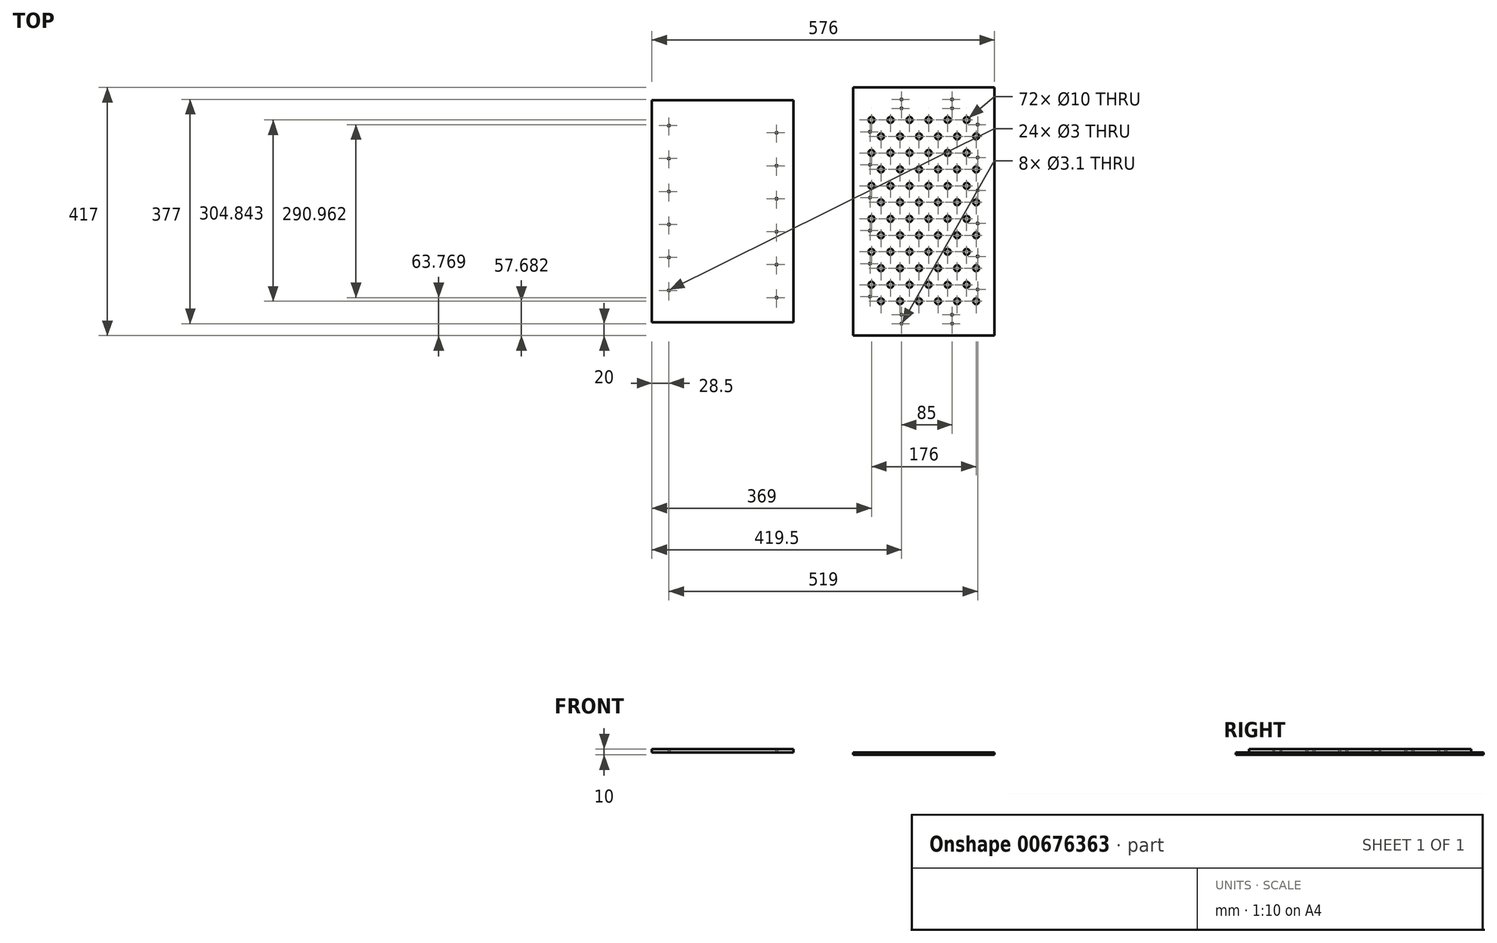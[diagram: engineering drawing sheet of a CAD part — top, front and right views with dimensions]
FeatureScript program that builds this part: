
annotation { "Feature Type Name" : "Feature", "Feature Type Description" : "" }
export const myFeature = defineFeature(function(context is Context, id is Id, definition is map)
    precondition{}
    {
        {
            var Q0;
            Q0=qCreatedBy(makeId("Top.planeOp"),FACE);
            var sketch = newSketch(context, id + "F0", { "sketchPlane" : qUnion([Q0])});
            skLineSegment(sketch, "E0.bottom", {"start": v(119, -186.75) * mm, "end": v(-119, -186.75) * mm});
            skLineSegment(sketch, "E0.top", {"start": v(119, 186.75) * mm, "end": v(-119, 186.75) * mm});
            skLineSegment(sketch, "E0.left", {"start": v(119, -186.75) * mm, "end": v(119, 186.75) * mm});
            skLineSegment(sketch, "E0.right", {"start": v(-119, -186.75) * mm, "end": v(-119, 186.75) * mm});
            skPoint(sketch, "E0.middle", {"position": v(0, 0) * mm});
            skCircle(sketch, "E1", {"center": v(-90.5, -133.36) * mm, "radius": 1.5 * mm});
            skCircle(sketch, "E2", {"center": v(-90.5, -77.93) * mm, "radius": 1.5 * mm});
            skCircle(sketch, "E3", {"center": v(90.5, -145.48) * mm, "radius": 1.5 * mm});
            skCircle(sketch, "E4", {"center": v(90.5, -90.06) * mm, "radius": 1.5 * mm});
            skPoint(sketch, "E5.endSnap0", {"position": v(0, 186.75) * mm});
            skCircle(sketch, "E6.0.1.0", {"center": v(-90.5, -22.5) * mm, "radius": 1.5 * mm});
            skCircle(sketch, "E6.0.2.0", {"center": v(-90.5, 32.92) * mm, "radius": 1.5 * mm});
            skCircle(sketch, "E6.0.3.0", {"center": v(-90.5, 88.34) * mm, "radius": 1.5 * mm});
            skCircle(sketch, "E6.0.4.0", {"center": v(-90.5, 143.77) * mm, "radius": 1.5 * mm});
            skLineSegment(sketch, "E6.direction1", {"start": v(-90.5, -77.93) * mm, "end": v(-65.5, -77.93) * mm, "construction": true});
            skLineSegment(sketch, "E6.direction2", {"start": v(-90.5, -77.93) * mm, "end": v(-90.5, -22.5) * mm, "construction": true});
            skCircle(sketch, "E7.0.1.0", {"center": v(90.5, -34.63) * mm, "radius": 1.5 * mm});
            skCircle(sketch, "E7.0.2.0", {"center": v(90.5, 20.8) * mm, "radius": 1.5 * mm});
            skCircle(sketch, "E7.0.3.0", {"center": v(90.5, 76.22) * mm, "radius": 1.5 * mm});
            skCircle(sketch, "E7.0.4.0", {"center": v(90.5, 131.64) * mm, "radius": 1.5 * mm});
            skLineSegment(sketch, "E7.direction1", {"start": v(90.5, -90.06) * mm, "end": v(115.5, -90.06) * mm, "construction": true});
            skLineSegment(sketch, "E7.direction2", {"start": v(90.5, -90.06) * mm, "end": v(90.5, -34.63) * mm, "construction": true});
            skSolve(sketch);
        }
        {
            var Q0;
            Q0 = qSketchRegion(id + "F0", true);
            extrude(context, id + "F1", {"entities" : qUnion([Q0]), "depth" : 6 * mm, "offsetDistance" : 25 * mm});
        }
        {
            var Q0;
            Q0=makeQuery(id+"F1.opExtrude","CAP_FACE",FACE,{"disambiguationData":[OSD([sQuery(id+"F0.wireOp",EDGE,"E0.bottom"),sQuery(id+"F0.wireOp",EDGE,"E0.top"),sQuery(id+"F0.wireOp",EDGE,"E0.left"),sQuery(id+"F0.wireOp",EDGE,"E0.right"),sQuery(id+"F0.wireOp",EDGE,"E1"),sQuery(id+"F0.wireOp",EDGE,"E2"),sQuery(id+"F0.wireOp",EDGE,"E3"),sQuery(id+"F0.wireOp",EDGE,"E4"),sQuery(id+"F0.wireOp",EDGE,"E6.0.1.0"),sQuery(id+"F0.wireOp",EDGE,"E6.0.2.0"),sQuery(id+"F0.wireOp",EDGE,"E6.0.3.0"),sQuery(id+"F0.wireOp",EDGE,"E6.0.4.0"),sQuery(id+"F0.wireOp",EDGE,"E7.0.1.0"),sQuery(id+"F0.wireOp",EDGE,"E7.0.2.0"),sQuery(id+"F0.wireOp",EDGE,"E7.0.3.0"),sQuery(id+"F0.wireOp",EDGE,"E7.0.4.0")])],"isStart":true});
            var sketch = newSketch(context, id + "F2", { "sketchPlane" : qUnion([Q0])});
            skLineSegment(sketch, "E8.bottom", {"start": v(457, -186.75) * mm, "end": v(219, -186.75) * mm});
            skLineSegment(sketch, "E8.top", {"start": v(457, 188.25) * mm, "end": v(219, 188.25) * mm});
            skLineSegment(sketch, "E8.left", {"start": v(457, -186.75) * mm, "end": v(457, 188.25) * mm});
            skLineSegment(sketch, "E8.right", {"start": v(219, -186.75) * mm, "end": v(219, 188.25) * mm});
            skPoint(sketch, "E8.middle", {"position": v(338, 0.75) * mm});
            skCircle(sketch, "E9", {"center": v(247.5, -133.36) * mm, "radius": 1.5 * mm});
            skCircle(sketch, "E10", {"center": v(247.5, -77.93) * mm, "radius": 1.5 * mm});
            skCircle(sketch, "E11", {"center": v(428.5, -145.48) * mm, "radius": 1.5 * mm});
            skCircle(sketch, "E12", {"center": v(428.5, -90.06) * mm, "radius": 1.5 * mm});
            skPoint(sketch, "E13.endSnap0", {"position": v(338, 188.25) * mm});
            skCircle(sketch, "E14.0.1.0", {"center": v(247.5, -22.5) * mm, "radius": 1.5 * mm});
            skCircle(sketch, "E14.0.2.0", {"center": v(247.5, 32.92) * mm, "radius": 1.5 * mm});
            skCircle(sketch, "E14.0.3.0", {"center": v(247.5, 88.34) * mm, "radius": 1.5 * mm});
            skCircle(sketch, "E14.0.4.0", {"center": v(247.5, 143.77) * mm, "radius": 1.5 * mm});
            skLineSegment(sketch, "E14.direction1", {"start": v(247.5, -77.93) * mm, "end": v(251.06, -77.93) * mm, "construction": true});
            skLineSegment(sketch, "E14.direction2", {"start": v(247.5, -77.93) * mm, "end": v(247.5, -22.5) * mm, "construction": true});
            skCircle(sketch, "E15.0.1.0", {"center": v(428.5, -34.63) * mm, "radius": 1.5 * mm});
            skCircle(sketch, "E15.0.2.0", {"center": v(428.5, 20.8) * mm, "radius": 1.5 * mm});
            skCircle(sketch, "E15.0.3.0", {"center": v(428.5, 76.22) * mm, "radius": 1.5 * mm});
            skCircle(sketch, "E15.0.4.0", {"center": v(428.5, 131.64) * mm, "radius": 1.5 * mm});
            skLineSegment(sketch, "E15.direction1", {"start": v(428.5, -90.06) * mm, "end": v(432.06, -90.06) * mm, "construction": true});
            skLineSegment(sketch, "E15.direction2", {"start": v(428.5, -90.06) * mm, "end": v(428.5, -34.63) * mm, "construction": true});
            skLineSegment(sketch, "E16", {"start": v(457, -186.75) * mm, "end": v(457, -207.75) * mm});
            skLineSegment(sketch, "E17", {"start": v(457, -207.75) * mm, "end": v(219, -207.75) * mm});
            skLineSegment(sketch, "E18", {"start": v(219, -207.75) * mm, "end": v(219, -186.75) * mm});
            skLineSegment(sketch, "E19", {"start": v(457, 188.25) * mm, "end": v(457, 209.25) * mm});
            skLineSegment(sketch, "E20", {"start": v(457, 209.25) * mm, "end": v(219, 209.25) * mm});
            skLineSegment(sketch, "E21", {"start": v(219, 209.25) * mm, "end": v(219, 188.25) * mm});
            skCircle(sketch, "E22", {"center": v(300.5, -187.75) * mm, "radius": 1.55 * mm});
            skCircle(sketch, "E23", {"center": v(300.5, -172.75) * mm, "radius": 1.55 * mm});
            skCircle(sketch, "E24", {"center": v(385.5, -187.75) * mm, "radius": 1.55 * mm});
            skCircle(sketch, "E25", {"center": v(385.5, -172.75) * mm, "radius": 1.55 * mm});
            skLineSegment(sketch, "E26", {"start": v(561.7, 0.75) * mm, "end": v(155.82, 0.75) * mm, "construction": true});
            skCircle(sketch, "E27.MirrorC", {"center": v(300.5, 174.25) * mm, "radius": 1.55 * mm});
            skCircle(sketch, "E28.MirrorC", {"center": v(300.5, 189.25) * mm, "radius": 1.55 * mm});
            skCircle(sketch, "E29.MirrorC", {"center": v(385.5, 189.25) * mm, "radius": 1.55 * mm});
            skCircle(sketch, "E30.MirrorC", {"center": v(385.5, 174.25) * mm, "radius": 1.55 * mm});
            skCircle(sketch, "E31", {"center": v(410, -153.28) * mm, "radius": 5 * mm});
            skCircle(sketch, "E32", {"center": v(426, -125.56) * mm, "radius": 5 * mm});
            skCircle(sketch, "E33.0.1.0", {"center": v(410, -97.85) * mm, "radius": 5 * mm});
            skCircle(sketch, "E33.0.1.1", {"center": v(426, -70.14) * mm, "radius": 5 * mm});
            skCircle(sketch, "E33.0.2.0", {"center": v(410, -42.42) * mm, "radius": 5 * mm});
            skCircle(sketch, "E33.0.2.1", {"center": v(426, -14.71) * mm, "radius": 5 * mm});
            skCircle(sketch, "E33.0.3.0", {"center": v(410, 13) * mm, "radius": 5 * mm});
            skCircle(sketch, "E33.0.3.1", {"center": v(426, 40.72) * mm, "radius": 5 * mm});
            skCircle(sketch, "E33.0.4.0", {"center": v(410, 68.43) * mm, "radius": 5 * mm});
            skCircle(sketch, "E33.0.4.1", {"center": v(426, 96.14) * mm, "radius": 5 * mm});
            skCircle(sketch, "E33.0.5.0", {"center": v(410, 123.85) * mm, "radius": 5 * mm});
            skCircle(sketch, "E33.0.5.1", {"center": v(426, 151.57) * mm, "radius": 5 * mm});
            skCircle(sketch, "E33.1.0.0", {"center": v(378, -153.28) * mm, "radius": 5 * mm});
            skCircle(sketch, "E33.1.0.1", {"center": v(394, -125.56) * mm, "radius": 5 * mm});
            skCircle(sketch, "E33.1.1.0", {"center": v(378, -97.85) * mm, "radius": 5 * mm});
            skCircle(sketch, "E33.1.1.1", {"center": v(394, -70.14) * mm, "radius": 5 * mm});
            skCircle(sketch, "E33.1.2.0", {"center": v(378, -42.42) * mm, "radius": 5 * mm});
            skCircle(sketch, "E33.1.2.1", {"center": v(394, -14.71) * mm, "radius": 5 * mm});
            skCircle(sketch, "E33.1.3.0", {"center": v(378, 13) * mm, "radius": 5 * mm});
            skCircle(sketch, "E33.1.3.1", {"center": v(394, 40.72) * mm, "radius": 5 * mm});
            skCircle(sketch, "E33.1.4.0", {"center": v(378, 68.43) * mm, "radius": 5 * mm});
            skCircle(sketch, "E33.1.4.1", {"center": v(394, 96.14) * mm, "radius": 5 * mm});
            skCircle(sketch, "E33.1.5.0", {"center": v(378, 123.85) * mm, "radius": 5 * mm});
            skCircle(sketch, "E33.1.5.1", {"center": v(394, 151.57) * mm, "radius": 5 * mm});
            skCircle(sketch, "E33.2.0.0", {"center": v(346, -153.28) * mm, "radius": 5 * mm});
            skCircle(sketch, "E33.2.0.1", {"center": v(362, -125.56) * mm, "radius": 5 * mm});
            skCircle(sketch, "E33.2.1.0", {"center": v(346, -97.85) * mm, "radius": 5 * mm});
            skCircle(sketch, "E33.2.1.1", {"center": v(362, -70.14) * mm, "radius": 5 * mm});
            skCircle(sketch, "E33.2.2.0", {"center": v(346, -42.42) * mm, "radius": 5 * mm});
            skCircle(sketch, "E33.2.2.1", {"center": v(362, -14.71) * mm, "radius": 5 * mm});
            skCircle(sketch, "E33.2.3.0", {"center": v(346, 13) * mm, "radius": 5 * mm});
            skCircle(sketch, "E33.2.3.1", {"center": v(362, 40.72) * mm, "radius": 5 * mm});
            skCircle(sketch, "E33.2.4.0", {"center": v(346, 68.43) * mm, "radius": 5 * mm});
            skCircle(sketch, "E33.2.4.1", {"center": v(362, 96.14) * mm, "radius": 5 * mm});
            skCircle(sketch, "E33.2.5.0", {"center": v(346, 123.85) * mm, "radius": 5 * mm});
            skCircle(sketch, "E33.2.5.1", {"center": v(362, 151.57) * mm, "radius": 5 * mm});
            skCircle(sketch, "E33.3.0.0", {"center": v(314, -153.28) * mm, "radius": 5 * mm});
            skCircle(sketch, "E33.3.0.1", {"center": v(330, -125.56) * mm, "radius": 5 * mm});
            skCircle(sketch, "E33.3.1.0", {"center": v(314, -97.85) * mm, "radius": 5 * mm});
            skCircle(sketch, "E33.3.1.1", {"center": v(330, -70.14) * mm, "radius": 5 * mm});
            skCircle(sketch, "E33.3.2.0", {"center": v(314, -42.42) * mm, "radius": 5 * mm});
            skCircle(sketch, "E33.3.2.1", {"center": v(330, -14.71) * mm, "radius": 5 * mm});
            skCircle(sketch, "E33.3.3.0", {"center": v(314, 13) * mm, "radius": 5 * mm});
            skCircle(sketch, "E33.3.3.1", {"center": v(330, 40.72) * mm, "radius": 5 * mm});
            skCircle(sketch, "E33.3.4.0", {"center": v(314, 68.43) * mm, "radius": 5 * mm});
            skCircle(sketch, "E33.3.4.1", {"center": v(330, 96.14) * mm, "radius": 5 * mm});
            skCircle(sketch, "E33.3.5.0", {"center": v(314, 123.85) * mm, "radius": 5 * mm});
            skCircle(sketch, "E33.3.5.1", {"center": v(330, 151.57) * mm, "radius": 5 * mm});
            skCircle(sketch, "E33.4.0.0", {"center": v(282, -153.28) * mm, "radius": 5 * mm});
            skCircle(sketch, "E33.4.0.1", {"center": v(298, -125.56) * mm, "radius": 5 * mm});
            skCircle(sketch, "E33.4.1.0", {"center": v(282, -97.85) * mm, "radius": 5 * mm});
            skCircle(sketch, "E33.4.1.1", {"center": v(298, -70.14) * mm, "radius": 5 * mm});
            skCircle(sketch, "E33.4.2.0", {"center": v(282, -42.42) * mm, "radius": 5 * mm});
            skCircle(sketch, "E33.4.2.1", {"center": v(298, -14.71) * mm, "radius": 5 * mm});
            skCircle(sketch, "E33.4.3.0", {"center": v(282, 13) * mm, "radius": 5 * mm});
            skCircle(sketch, "E33.4.3.1", {"center": v(298, 40.72) * mm, "radius": 5 * mm});
            skCircle(sketch, "E33.4.4.0", {"center": v(282, 68.43) * mm, "radius": 5 * mm});
            skCircle(sketch, "E33.4.4.1", {"center": v(298, 96.14) * mm, "radius": 5 * mm});
            skCircle(sketch, "E33.4.5.0", {"center": v(282, 123.85) * mm, "radius": 5 * mm});
            skCircle(sketch, "E33.4.5.1", {"center": v(298, 151.57) * mm, "radius": 5 * mm});
            skCircle(sketch, "E33.5.0.0", {"center": v(250, -153.28) * mm, "radius": 5 * mm});
            skCircle(sketch, "E33.5.0.1", {"center": v(266, -125.56) * mm, "radius": 5 * mm});
            skCircle(sketch, "E33.5.1.0", {"center": v(250, -97.85) * mm, "radius": 5 * mm});
            skCircle(sketch, "E33.5.1.1", {"center": v(266, -70.14) * mm, "radius": 5 * mm});
            skCircle(sketch, "E33.5.2.0", {"center": v(250, -42.42) * mm, "radius": 5 * mm});
            skCircle(sketch, "E33.5.2.1", {"center": v(266, -14.71) * mm, "radius": 5 * mm});
            skCircle(sketch, "E33.5.3.0", {"center": v(250, 13) * mm, "radius": 5 * mm});
            skCircle(sketch, "E33.5.3.1", {"center": v(266, 40.72) * mm, "radius": 5 * mm});
            skCircle(sketch, "E33.5.4.0", {"center": v(250, 68.43) * mm, "radius": 5 * mm});
            skCircle(sketch, "E33.5.4.1", {"center": v(266, 96.14) * mm, "radius": 5 * mm});
            skCircle(sketch, "E33.5.5.0", {"center": v(250, 123.85) * mm, "radius": 5 * mm});
            skCircle(sketch, "E33.5.5.1", {"center": v(266, 151.57) * mm, "radius": 5 * mm});
            skLineSegment(sketch, "E33.direction1", {"start": v(410, -153.28) * mm, "end": v(378, -153.28) * mm, "construction": true});
            skLineSegment(sketch, "E33.direction2", {"start": v(410, -153.28) * mm, "end": v(410, -97.85) * mm, "construction": true});
            skSolve(sketch);
        }
        {
            var Q0;
            Q0=makeQuery(id+"F2.imprint","IMPRINT",FACE,{"disambiguationData":[TD([[makeQuery(id+"F2.imprint","IMPRINT",EDGE,{"derivedFrom":sQuery(id+"F2.wireOp",EDGE,"E8.bottom")}),1.0]])]});
            var Q1;
            Q1=makeQuery(id+"F2.imprint","IMPRINT",FACE,{"disambiguationData":[TD([[makeQuery(id+"F2.imprint","IMPRINT",EDGE,{"derivedFrom":sQuery(id+"F2.wireOp",EDGE,"E8.top")}),-1.0]])]});
            var Q2;
            {var subQ7=sQuery(id+"F2.wireOp",EDGE,"E8.left");Q2=makeQuery(id+"F2.imprint","IMPRINT",FACE,{"disambiguationData":[TD([[makeQuery(id+"F2.imprint","IMPRINT",EDGE,{"derivedFrom":subQ7}),1.0]])]});}
            extrude(context, id + "F3", {"entities" : qUnion([Q0, Q1, Q2]), "depth" : 4 * mm, "offsetDistance" : 25 * mm});
        }
    });
